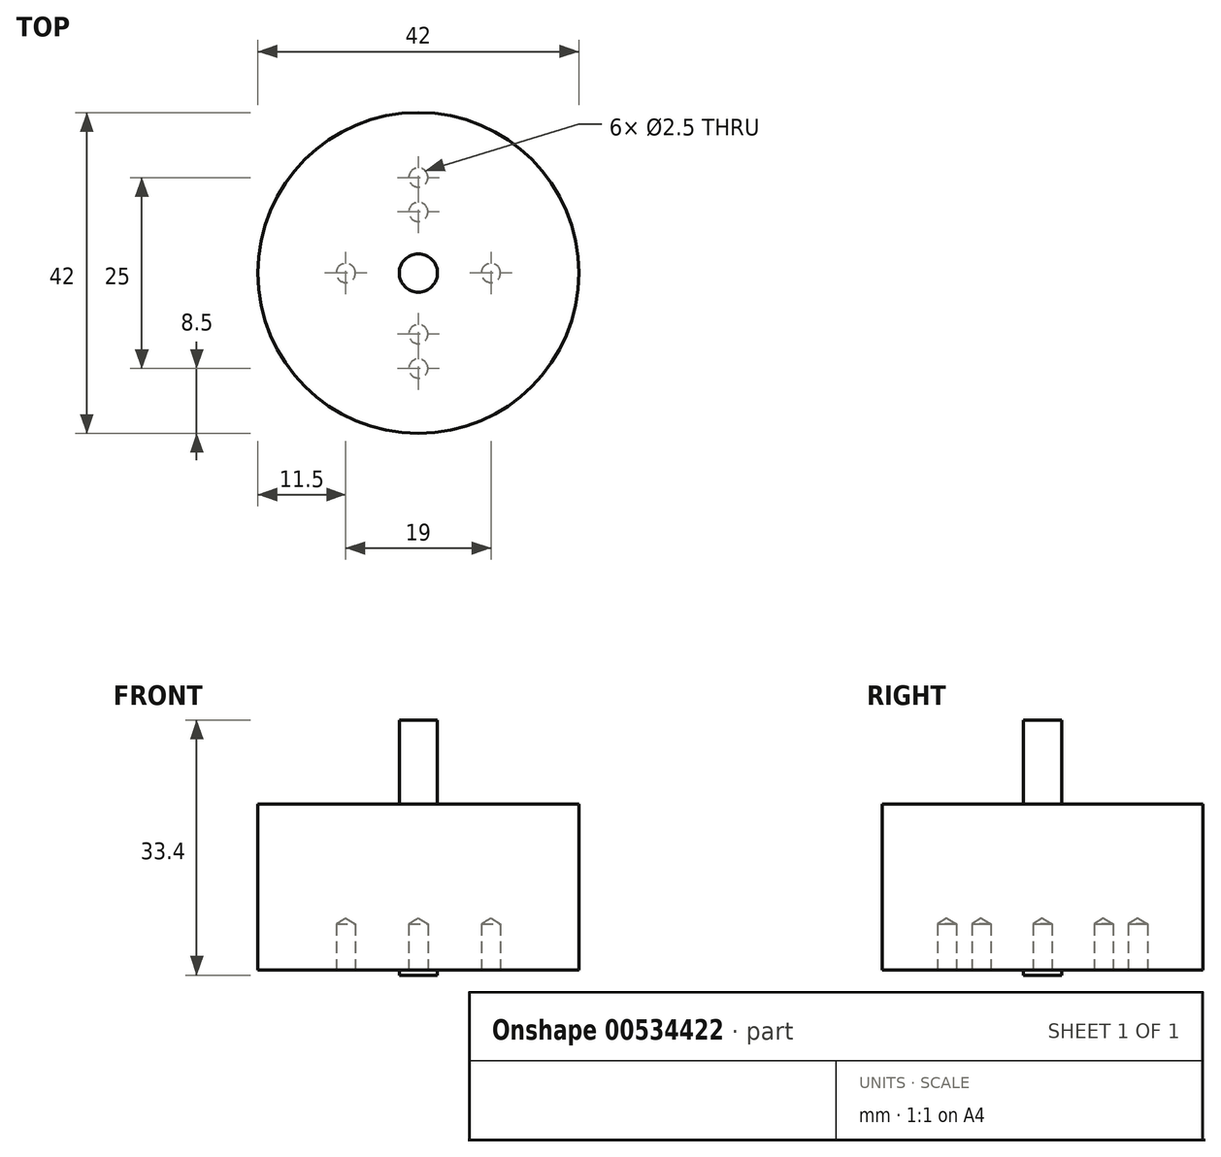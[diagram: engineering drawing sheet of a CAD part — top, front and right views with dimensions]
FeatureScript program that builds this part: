
annotation { "Feature Type Name" : "Feature", "Feature Type Description" : "" }
export const myFeature = defineFeature(function(context is Context, id is Id, definition is map)
    precondition{}
    {
        {
            var Q0;
            Q0=qCreatedBy(makeId("Front.planeOp"),FACE);
            var sketch = newSketch(context, id + "F0", { "sketchPlane" : qUnion([Q0])});
            skLineSegment(sketch, "E0.bottom", {"start": v(0, 0) * mm, "end": v(21, 0) * mm});
            skLineSegment(sketch, "E0.top", {"start": v(0, 21.7) * mm, "end": v(21, 21.7) * mm});
            skLineSegment(sketch, "E0.left", {"start": v(0, 0) * mm, "end": v(0, 21.7) * mm});
            skLineSegment(sketch, "E0.right", {"start": v(21, 0) * mm, "end": v(21, 21.7) * mm});
            skSolve(sketch);
        }
        {
            var Q0;
            Q0=makeQuery(id+"F0.imprint","IMPRINT",FACE,{"disambiguationData":[TD([[makeQuery(id+"F0.imprint","IMPRINT",EDGE,{"derivedFrom":sQuery(id+"F0.wireOp",EDGE,"E0.bottom")}),1.0]])]});
            var Q1;
            Q1=sQuery(id+"F0.wireOp",EDGE,"E0.left");
            revolve(context, id + "F1", {"entities" : qUnion([Q0]), "axis" : qUnion([Q1]), "revolveType" : RevolveType.FULL});
        }
        {
            var Q0;
            Q0=makeQuery(id+"F1.opRevolve","SWEPT_FACE",FACE,{"disambiguationData":[OSD([sQuery(id+"F0.wireOp",EDGE,"E0.bottom")])]});
            var sketch = newSketch(context, id + "F2", { "sketchPlane" : qUnion([Q0])});
            skPoint(sketch, "E1", {"position": v(0, 8) * mm});
            skPoint(sketch, "E2", {"position": v(-9.5, 0) * mm});
            skPoint(sketch, "E3", {"position": v(0, -8) * mm});
            skPoint(sketch, "E4", {"position": v(9.5, 0) * mm});
            skPoint(sketch, "E5", {"position": v(0, 12.5) * mm});
            skPoint(sketch, "E6", {"position": v(0, -12.5) * mm});
            skLineSegment(sketch, "E7", {"start": v(9.5, 0) * mm, "end": v(0, 0) * mm});
            skLineSegment(sketch, "E8", {"start": v(-9.5, 0) * mm, "end": v(0, 0) * mm});
            skLineSegment(sketch, "E9", {"start": v(0, -8) * mm, "end": v(0, 0) * mm});
            skLineSegment(sketch, "E10", {"start": v(0, 8) * mm, "end": v(0, 0) * mm});
            skLineSegment(sketch, "E11", {"start": v(0, 12.5) * mm, "end": v(0, 8) * mm});
            skLineSegment(sketch, "E12", {"start": v(0, -12.5) * mm, "end": v(0, -8) * mm});
            skSolve(sketch);
        }
        {
            var Q0;
            Q0=sQuery(id+"F2.wireOp",VERTEX,"E5");
            var Q1;
            Q1=sQuery(id+"F2.wireOp",VERTEX,"E1");
            var Q2;
            Q2=sQuery(id+"F2.wireOp",VERTEX,"E2");
            var Q3;
            Q3=sQuery(id+"F2.wireOp",VERTEX,"E4");
            var Q4;
            Q4=sQuery(id+"F2.wireOp",VERTEX,"E3");
            var Q5;
            Q5=sQuery(id+"F2.wireOp",VERTEX,"E6");
            var Q6;
            Q6=makeQuery(id+"F1.opRevolve","SWEPT_BODY",BODY,{"disambiguationData":[OSD([sQuery(id+"F0.wireOp",EDGE,"E0.bottom"),sQuery(id+"F0.wireOp",EDGE,"E0.top"),sQuery(id+"F0.wireOp",EDGE,"E0.left"),sQuery(id+"F0.wireOp",EDGE,"E0.right")])]});
            hole(context, id + "F3", {"style" : HoleStyle.SIMPLE, "endStyle" : HoleEndStyle.BLIND, "standardTappedOrClearance" : lookupTablePath({ "standard" : "ISO", "engagement" : "75%", "pitch" : "0.5 mm", "size" : "M3", "type" : "Tapped" }), "standardBlindInLast" : lookupTablePath({ "standard" : "ISO", "engagement" : "75%", "pitch" : "0.5 mm", "size" : "M3", "type" : "Tapped" }), "holeDiameter" : 2.5 * mm, "showTappedDepth" : true, "holeDepth" : 6 * mm, "tappedDepth" : 3 * mm, "tapClearance" : 6, "locations" : qUnion([Q0, Q1, Q2, Q3, Q4, Q5]), "scope" : qUnion([Q6]), "majorDiameter" : 3 * mm});
        }
        {
            var Q0;
            Q0=makeQuery(id+"F1.opRevolve","SWEPT_FACE",FACE,{"disambiguationData":[OSD([sQuery(id+"F0.wireOp",EDGE,"E0.top")])]});
            var sketch = newSketch(context, id + "F4", { "sketchPlane" : qUnion([Q0])});
            skPoint(sketch, "E13", {"position": v(0, 0) * mm});
            skCircle(sketch, "E14", {"center": v(0, 0) * mm, "radius": 2.5 * mm});
            skSolve(sketch);
        }
        {
            var Q0;
            Q0=makeQuery(id+"F4.imprint","IMPRINT",FACE,{"disambiguationData":[TD([[makeQuery(id+"F4.imprint","IMPRINT",EDGE,{"derivedFrom":sQuery(id+"F4.wireOp",EDGE,"E14")}),1.0]])]});
            extrude(context, id + "F5", {"entities" : qUnion([Q0]), "operationType" : NewBodyOperationType.ADD, "depth" : 11 * mm, "offsetDistance" : 25.4 * mm});
        }
        {
            var Q0;
            Q0=makeQuery(id+"F1.opRevolve","SWEPT_FACE",FACE,{"disambiguationData":[OSD([sQuery(id+"F0.wireOp",EDGE,"E0.bottom")])]});
            var sketch = newSketch(context, id + "F6", { "sketchPlane" : qUnion([Q0])});
            skCircle(sketch, "E15", {"center": v(0, 0) * mm, "radius": 2.5 * mm});
            skSolve(sketch);
        }
        {
            var Q0;
            Q0=makeQuery(id+"F6.imprint","IMPRINT",FACE,{"disambiguationData":[TD([[makeQuery(id+"F6.imprint","IMPRINT",EDGE,{"derivedFrom":sQuery(id+"F6.wireOp",EDGE,"E15")}),1.0]])]});
            extrude(context, id + "F7", {"entities" : qUnion([Q0]), "operationType" : NewBodyOperationType.ADD, "depth" : .7 * mm, "offsetDistance" : 25.4 * mm});
        }
    });
